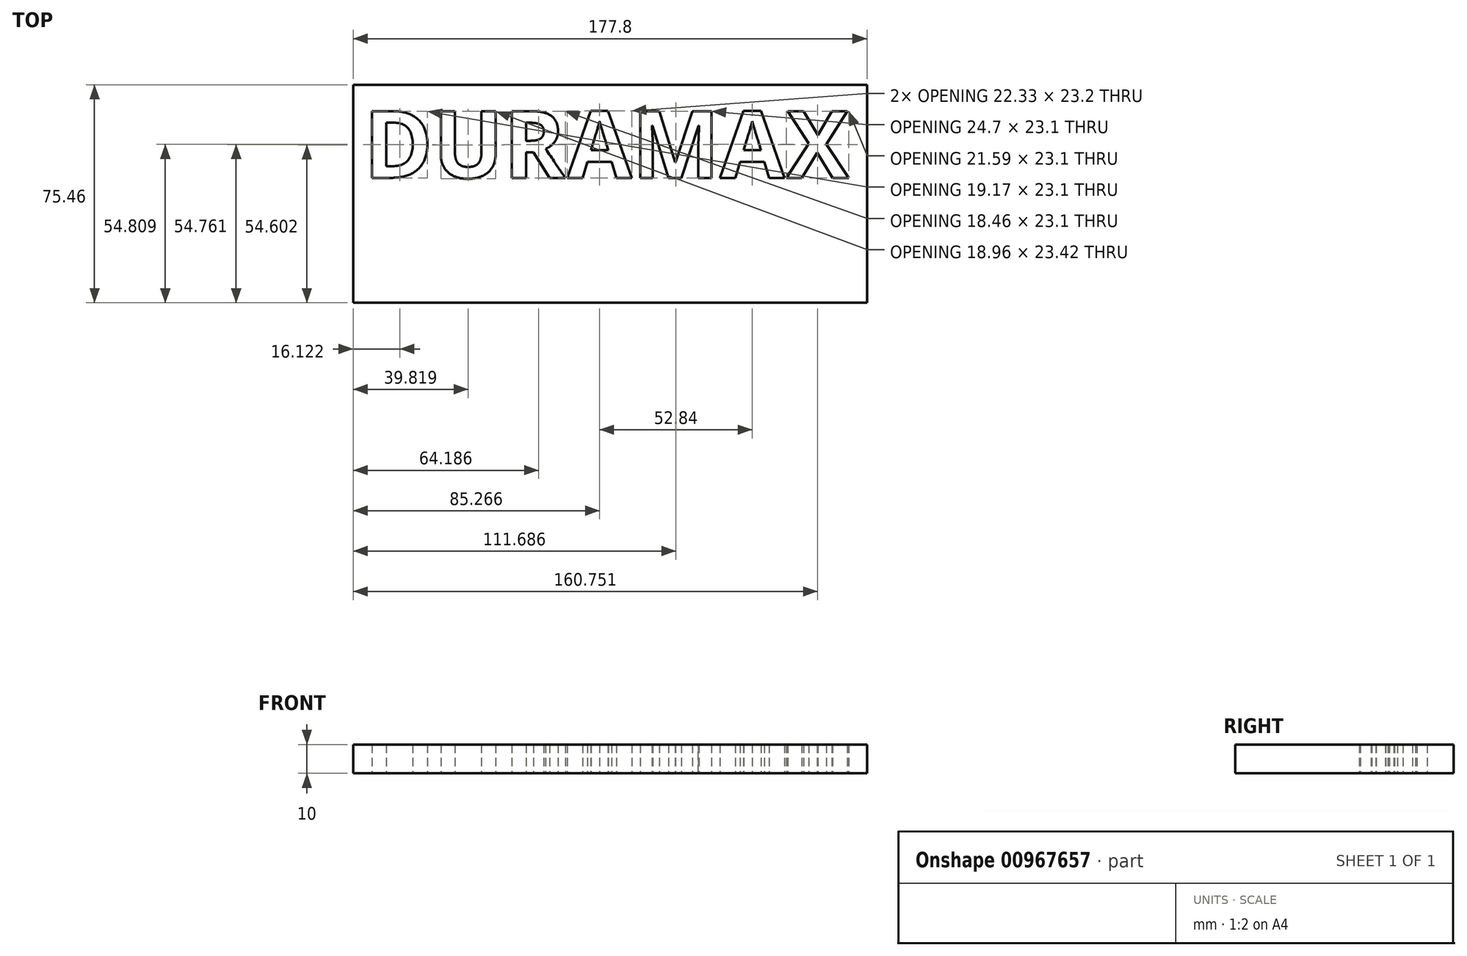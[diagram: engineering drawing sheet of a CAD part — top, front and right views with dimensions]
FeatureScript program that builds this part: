
annotation { "Feature Type Name" : "Feature", "Feature Type Description" : "" }
export const myFeature = defineFeature(function(context is Context, id is Id, definition is map)
    precondition{}
    {
        {
            var Q0;
            Q0=qCreatedBy(makeId("Top.planeOp"),FACE);
            var sketch = newSketch(context, id + "F0", { "sketchPlane" : qUnion([Q0])});
            skLineSegment(sketch, "E0.bottom", {"start": v(50.92, -18.58) * mm, "end": v(-126.88, -18.58) * mm});
            skLineSegment(sketch, "E0.top", {"start": v(50.92, 56.88) * mm, "end": v(-126.88, 56.88) * mm});
            skLineSegment(sketch, "E0.left", {"start": v(50.92, -18.58) * mm, "end": v(50.92, 56.88) * mm});
            skLineSegment(sketch, "E0.right", {"start": v(-126.88, -18.58) * mm, "end": v(-126.88, 56.88) * mm});
            skPoint(sketch, "E0.middle", {"position": v(-37.98, 19.15) * mm});
            skSolve(sketch);
        }
        {
            var Q0;
            Q0=makeQuery(id+"F0.imprint","IMPRINT",FACE,{"disambiguationData":[TD([[makeQuery(id+"F0.imprint","IMPRINT",EDGE,{"derivedFrom":sQuery(id+"F0.wireOp",EDGE,"E0.bottom")}),-1.0]])]});
            extrude(context, id + "F1", {"entities" : qUnion([Q0]), "depth" : 10 * mm, "offsetDistance" : 25 * mm});
        }
        {
            var Q0;
            Q0=qCreatedBy(makeId("Top.planeOp"),FACE);
            var sketch = newSketch(context, id + "F2", { "sketchPlane" : qUnion([Q0])});
            skText(sketch, "E1", { "text": "DURAMAX ", "fontName": "OpenSans-Bold.ttf"});
            const initialGuessF2  = {"E1": [-0.12325, 0.02463, 1, 0, 0.0233]};
            skSetInitialGuess(sketch, initialGuessF2);
            skSolve(sketch);
        }
        {
            var Q0;
            Q0 = qSketchRegion(id + "F2", true);
            extrude(context, id + "F3", {"entities" : qUnion([Q0]), "operationType" : NewBodyOperationType.REMOVE, "depth" : 25 * mm, "offsetDistance" : 25 * mm});
        }
    });
